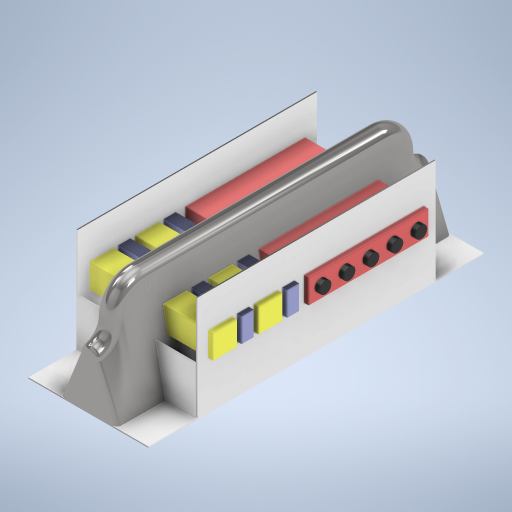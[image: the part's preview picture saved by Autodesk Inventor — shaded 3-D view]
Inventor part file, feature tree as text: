
AUTODESK INVENTOR PART (.ipt)
format: ipt  version: 2023 (Build 270158000, 158)  size: 909,312 bytes
history: native  units: mm
features: sketch x19, extrude x10, fillet x6, plane x4, loft x4, other x4, sweep x2
ambient origin geometry x8: Origin, YZ Plane, XZ Plane, XY Plane, X Axis, Y Axis, Z Axis, Center Point
bodies: Solid1 (feature_tree)
feature tree (49):
  extrude  "Extrusion1"  Depth=120.0mm
  plane  "Work Plane1"
  sketch  "Sketch2"  dims[d3=500.0mm d4=0.0mm d5=100.0mm]
  sketch  "Sketch3"  dims[d7=50.0mm d8=50.0mm]
  plane  "Work Plane2"
  plane  "Work Plane3"
  sketch  "Sketch4"  dims[d11=-500.0mm d12=-600.0mm d13=40.0mm]
  sketch  "Sketch5"  dims[d14=40.0mm d15=50.0mm]
  sketch  "Sketch6"  dims[d16=50.0mm d17=0.0mm d18=0.0mm]
  sweep  "Sweep1"
  sweep  "Sweep2"
  extrude  "Extrusion2"  Depth=40.0mm
  sketch  "Sketch8"  dims[d23=100.0mm d24=0.0mm d25=90.0deg]
  sketch  "Sketch9"  dims[d26=0.0mm d27=90.0deg d28=100.0mm d29=0.0mm d30=90.0deg d31=0.0mm d32=90.0deg d33=0.0mm d34=90.0deg d37=0.0mm d38=90.0deg d39=0.0mm d40=90.0deg d41=0.0mm d42=90.0deg]
  loft  "Loft1"
  loft  "Loft2"
  loft  "Loft3"
  loft  "Loft4"
  extrude  "Extrusion3"  Depth=100.0mm
  fillet  "Fillet1"  [1 undecoded]
  fillet  "Fillet2"  [1 undecoded]
  fillet  "Fillet3"  [1 undecoded]
  fillet  "Fillet4"  [1 undecoded]
  fillet  "Fillet5"  [1 undecoded]
  fillet  "Fillet6"  [1 undecoded]
  extrude  "Extrusion4"  Depth=250.0mm
  plane  "Work Plane4"
  extrude  "Extrusion5"  Depth=220.0mm
  extrude  "Extrusion6"  Depth=220.0mm
  extrude  "Extrusion7"  Depth=10.0mm
  extrude  "Extrusion8"  Depth=10.0mm
  extrude  "Extrusion9"  Depth=10.0mm
  extrude  "Extrusion10"  Depth=250.0mm
  sketch  "Sketch1"  dims[d0=40.0mm d1=120.0mm]
  sketch  "Sketch7"  dims[d19=0.0mm d20=0.0mm d21=0.0mm d22=0.0mm]
  other  "Edges1"
  sketch  "Sketch10"  dims[d43=250.0mm d44=1.0mm]
  other  "Edges2"
  sketch  "Sketch11"  dims[d45=2.5mm d46=220.0mm]
  sketch  "Sketch12"  dims[d47=2.5mm d48=220.0mm]
  other  "Edges4"
  other  "Edges5"
  sketch  "Sketch13"  dims[d49=100.0mm d50=600.0mm d51=0.0mm d52=0.0mm d53=10.0mm]
  sketch  "Sketch14"  dims[d54=10.0mm d55=10.0mm]
  sketch  "Sketch15"  dims[d56=10.0mm d57=10.0mm]
  sketch  "Sketch17"  dims[d58=10.0mm d59=250.0mm]
  sketch  "Sketch18"  dims[d60=2.5mm]
  sketch  "Sketch19"  dims[d61=100.0mm]
  sketch  "Sketch20"  dims[d62=2.5mm d63=100.0mm d64=2.5mm d65=0.0mm d66=0.0mm d67=125.0mm d68=50.0mm d69=50.0mm d70=25.0mm d71=50.0mm d72=25.0mm d73=250.0mm d74=10.0mm d75=260.0mm d76=0.0mm d77=0.0mm d78=25.0mm d79=10.0mm d80=280.0mm d81=0.0mm d82=0.0mm d83=10.0mm d84=0.0mm d85=10.0mm d86=0.0mm d87=10.0mm d88=0.0mm d89=10.0mm d90=0.0mm d91=85.0mm d92=120.0mm d93=180.0mm d94=25.0mm d95=25.0mm d96=25.0mm d97=25.0mm d98=25.0mm d99=25.0mm d100=50.0mm d101=25.0mm d102=25.0mm d103=25.0mm d104=25.0mm d105=50.0mm d106=50.0mm]
note: 6 required parameter values undecoded (feature->parameter linkage not recoverable at this tier; creation-order binding heuristic only, values carry confidence <= 0.55)
